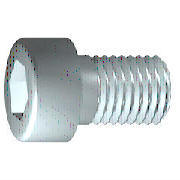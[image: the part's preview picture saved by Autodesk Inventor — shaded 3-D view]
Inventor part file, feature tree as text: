
AUTODESK INVENTOR PART (.ipt)
format: ipt  version: 2023.2 (Build 272271030, 271C)  size: 195,072 bytes
history: native  units: mm (DEFAULTED — no unit token found)
features: sketch x2, other x1, extrude x1, plane x1, fillet x1
ambient origin geometry x7: Origin, YZ Plane, XY Plane, X Axis, Y Axis, Z Axis, Center Point
bodies: Solid1 (feature_tree)
feature tree (6):
  other  "Körper"
  extrude  "Loch"  Depth=3.0mm
  plane  "Work Plane1"
  fillet  "Fillet2"  Radius=3.0mm
  sketch  "Skizze1"  dims[d1=6.75mm d2=0.306825mm d3=3.0mm]
  sketch  "Skizze2"  dims[d4=1.3mm d5=60.0deg d6=3.0mm d7=3.0mm d8=2.886751mm d9=5.5mm d10=90.0deg d11=10.0mm d12=0.0mm d13=6.75mm d14=0.0mm d15=0.306725mm d16=0.306725mm d17=0.3mm d19=0.0mm d26=8.0mm d27=45.0deg d28=0.0mm d29=0.0mm d30=0.1mm]
